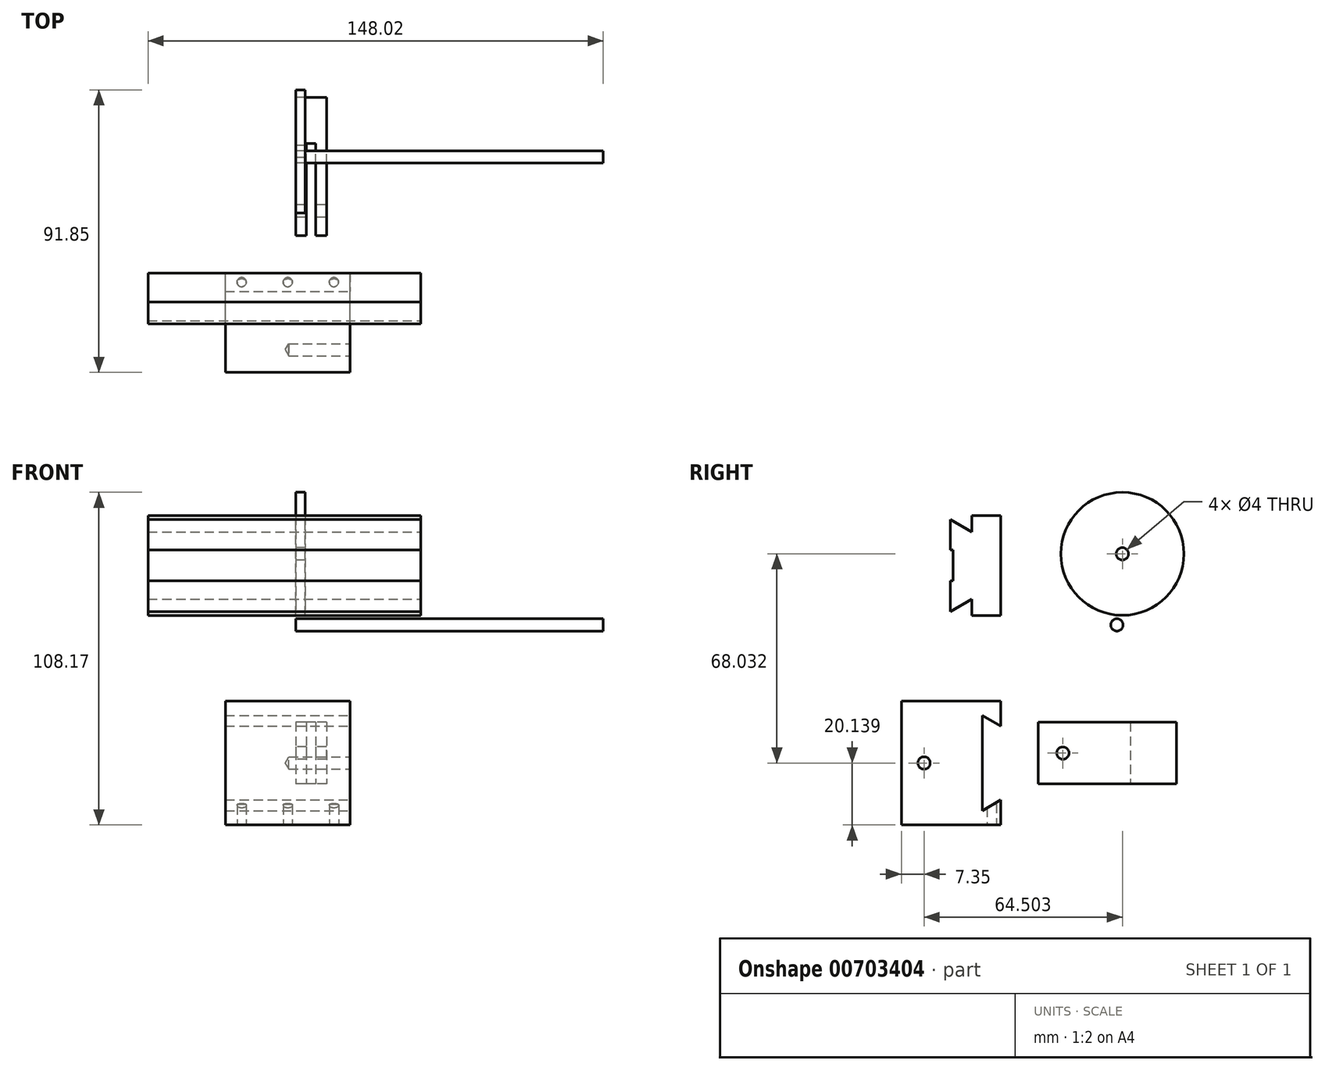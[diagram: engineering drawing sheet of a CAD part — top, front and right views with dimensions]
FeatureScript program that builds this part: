
annotation { "Feature Type Name" : "Feature", "Feature Type Description" : "" }
export const myFeature = defineFeature(function(context is Context, id is Id, definition is map)
    precondition{}
    {
        {
            var Q0;
            Q0=qCreatedBy(makeId("Front.planeOp"),FACE);
            var sketch = newSketch(context, id + "F0", { "sketchPlane" : qUnion([Q0])});
            skLineSegment(sketch, "E0.bottom", {"start": v(-48.02, 50.48) * mm, "end": v(40.65, 50.48) * mm});
            skLineSegment(sketch, "E0.top", {"start": v(-48.02, 17.98) * mm, "end": v(40.65, 17.98) * mm});
            skLineSegment(sketch, "E0.left", {"start": v(-48.02, 50.48) * mm, "end": v(-48.02, 17.98) * mm});
            skLineSegment(sketch, "E0.right", {"start": v(40.65, 50.48) * mm, "end": v(40.65, 17.98) * mm});
            skSolve(sketch);
        }
        {
            var Q0;
            Q0=makeQuery(id+"F0.imprint","IMPRINT",FACE,{"disambiguationData":[TD([[makeQuery(id+"F0.imprint","IMPRINT",EDGE,{"derivedFrom":sQuery(id+"F0.wireOp",EDGE,"E0.bottom")}),-1.0]])]});
            extrude(context, id + "F1", {"entities" : qUnion([Q0]), "depth" : 16.5 * mm, "offsetDistance" : 25 * mm});
        }
        {
            var Q0;
            Q0=qCreatedBy(makeId("Front.planeOp"),FACE);
            var sketch = newSketch(context, id + "F2", { "sketchPlane" : qUnion([Q0])});
            skLineSegment(sketch, "E1.bottom", {"start": v(-22.87, -9.87) * mm, "end": v(17.73, -9.87) * mm});
            skLineSegment(sketch, "E1.top", {"start": v(-22.87, -50.14) * mm, "end": v(17.73, -50.14) * mm});
            skLineSegment(sketch, "E1.left", {"start": v(-22.87, -9.87) * mm, "end": v(-22.87, -50.14) * mm});
            skLineSegment(sketch, "E1.right", {"start": v(17.73, -9.87) * mm, "end": v(17.73, -50.14) * mm});
            skSolve(sketch);
        }
        {
            var Q0;
            Q0=makeQuery(id+"F2.imprint","IMPRINT",FACE,{"disambiguationData":[TD([[makeQuery(id+"F2.imprint","IMPRINT",EDGE,{"derivedFrom":sQuery(id+"F2.wireOp",EDGE,"E1.bottom")}),-1.0]])]});
            extrude(context, id + "F3", {"entities" : qUnion([Q0]), "depth" : 32.35 * mm, "offsetDistance" : 25 * mm});
        }
        {
            var Q0;
            Q0=makeQuery(id+"F3.opExtrude","SWEPT_FACE",FACE,{"disambiguationData":[OSD([sQuery(id+"F2.wireOp",EDGE,"E1.right")])]});
            var sketch = newSketch(context, id + "F4", { "sketchPlane" : qUnion([Q0])});
            skLineSegment(sketch, "E2", {"start": v(0, -17.97) * mm, "end": v(-6, -14.5) * mm});
            skLineSegment(sketch, "E3", {"start": v(-6, -14.5) * mm, "end": v(-6, -45.5) * mm});
            skLineSegment(sketch, "E4", {"start": v(-6, -45.5) * mm, "end": v(0, -42.04) * mm});
            skLineSegment(sketch, "E5", {"start": v(0, -30) * mm, "end": v(-32.35, -30) * mm, "construction": true});
            skPoint(sketch, "E6", {"position": v(-25, -30) * mm});
            skPoint(sketch, "E6.positionSnap0", {"position": v(-25, -30) * mm});
            skLineSegment(sketch, "E7", {"start": v(0, -17.97) * mm, "end": v(0, -42.04) * mm});
            skSolve(sketch);
        }
        {
            var Q0;
            {var subQ0=sQuery(id+"F4.wireOp",EDGE,"E2");Q0=makeQuery(id+"F4.imprint","IMPRINT",FACE,{"disambiguationData":[TD([[makeQuery(id+"F4.imprint","IMPRINT",EDGE,{"derivedFrom":subQ0}),1.0]])]});}
            extrude(context, id + "F5", {"entities" : qUnion([Q0]), "operationType" : NewBodyOperationType.REMOVE, "endBound" : BoundingType.UP_TO_NEXT, "oppositeDirection" : true, "depth" : 25 * mm, "offsetDistance" : 25 * mm});
        }
        {
            var Q0;
            Q0=makeQuery(id+"F1.opExtrude","SWEPT_FACE",FACE,{"disambiguationData":[OSD([sQuery(id+"F0.wireOp",EDGE,"E0.right")])]});
            var sketch = newSketch(context, id + "F6", { "sketchPlane" : qUnion([Q0])});
            skLineSegment(sketch, "E8", {"start": v(-16.5, 50.48) * mm, "end": v(-9.5, 50.48) * mm, "construction": true});
            skLineSegment(sketch, "E9", {"start": v(-16.5, 50.48) * mm, "end": v(-16.5, 49.23) * mm, "construction": true});
            skLineSegment(sketch, "E10", {"start": v(-16.5, 19.23) * mm, "end": v(-16.5, 17.98) * mm, "construction": true});
            skLineSegment(sketch, "E11", {"start": v(-16.5, 17.98) * mm, "end": v(-9.5, 17.98) * mm, "construction": true});
            skLineSegment(sketch, "E12", {"start": v(-16.5, 49.23) * mm, "end": v(-9.5, 45.18) * mm});
            skLineSegment(sketch, "E13", {"start": v(-9.5, 45.18) * mm, "end": v(-9.5, 50.48) * mm});
            skLineSegment(sketch, "E14", {"start": v(-16.5, 19.23) * mm, "end": v(-9.5, 23.27) * mm});
            skLineSegment(sketch, "E15", {"start": v(-9.5, 23.27) * mm, "end": v(-9.5, 17.98) * mm});
            skLineSegment(sketch, "E16", {"start": v(-16.5, 19.23) * mm, "end": v(-16.5, 49.23) * mm});
            skSolve(sketch);
        }
        {
            var Q0;
            {var subQ0=sQuery(id+"F6.wireOp",EDGE,"E12");Q0=makeQuery(id+"F6.imprint","IMPRINT",FACE,{"disambiguationData":[TD([[makeQuery(id+"F6.imprint","IMPRINT",EDGE,{"derivedFrom":subQ0}),1.0]])]});}
            var Q1;
            {var subQ0=sQuery(id+"F6.wireOp",EDGE,"E14");Q1=makeQuery(id+"F6.imprint","IMPRINT",FACE,{"disambiguationData":[TD([[makeQuery(id+"F6.imprint","IMPRINT",EDGE,{"derivedFrom":subQ0}),-1.0]])]});}
            extrude(context, id + "F7", {"entities" : qUnion([Q0, Q1]), "operationType" : NewBodyOperationType.REMOVE, "endBound" : BoundingType.UP_TO_NEXT, "oppositeDirection" : true, "depth" : 25 * mm, "offsetDistance" : 25 * mm});
        }
        {
            var Q0;
            Q0=makeQuery(id+"F1.opExtrude","CAP_FACE",FACE,{"disambiguationData":[OSD([sQuery(id+"F0.wireOp",EDGE,"E0.bottom"),sQuery(id+"F0.wireOp",EDGE,"E0.top"),sQuery(id+"F0.wireOp",EDGE,"E0.left"),sQuery(id+"F0.wireOp",EDGE,"E0.right")])],"isStart":false});
            var sketch = newSketch(context, id + "F8", { "sketchPlane" : qUnion([Q0])});
            skLineSegment(sketch, "E17", {"start": v(-48.02, 34.23) * mm, "end": v(40.65, 34.23) * mm, "construction": true});
            skLineSegment(sketch, "E18.bottom", {"start": v(-48.02, 39.23) * mm, "end": v(40.65, 39.23) * mm});
            skLineSegment(sketch, "E18.top", {"start": v(-48.02, 29.23) * mm, "end": v(40.65, 29.23) * mm});
            skLineSegment(sketch, "E18.left", {"start": v(-48.02, 39.23) * mm, "end": v(-48.02, 29.23) * mm});
            skLineSegment(sketch, "E18.right", {"start": v(40.65, 39.23) * mm, "end": v(40.65, 29.23) * mm});
            skPoint(sketch, "E18.middle", {"position": v(-3.68, 34.23) * mm});
            skSolve(sketch);
        }
        {
            var Q0;
            Q0=makeQuery(id+"F8.imprint","IMPRINT",FACE,{"disambiguationData":[TD([[makeQuery(id+"F8.imprint","IMPRINT",EDGE,{"derivedFrom":sQuery(id+"F8.wireOp",EDGE,"E18.bottom")}),-1.0]])]});
            extrude(context, id + "F9", {"entities" : qUnion([Q0]), "operationType" : NewBodyOperationType.REMOVE, "oppositeDirection" : true, "depth" : 1 * mm, "offsetDistance" : 25 * mm});
        }
        {
            var Q0;
            Q0=makeQuery(id+"F3.opExtrude","SWEPT_FACE",FACE,{"disambiguationData":[OSD([sQuery(id+"F2.wireOp",EDGE,"E1.top")])]});
            var sketch = newSketch(context, id + "F10", { "sketchPlane" : qUnion([Q0])});
            skLineSegment(sketch, "E19", {"start": v(-22.87, 3) * mm, "end": v(17.73, 3) * mm, "construction": true});
            skPoint(sketch, "E20", {"position": v(-2.57, 3) * mm});
            skLineSegment(sketch, "E21", {"start": v(-2.57, 3) * mm, "end": v(-17.57, 3) * mm, "construction": true});
            skLineSegment(sketch, "E22", {"start": v(-2.57, 3) * mm, "end": v(12.43, 3) * mm, "construction": true});
            skSolve(sketch);
        }
        {
            var Q0;
            Q0=sQuery(id+"F10.wireOp",VERTEX,"E20");
            var Q1;
            Q1=sQuery(id+"F10.wireOp",VERTEX,"E22.end");
            var Q2;
            Q2=sQuery(id+"F10.wireOp",VERTEX,"E21.end");
            var Q3;
            Q3=makeQuery(id+"F3.opExtrude","SWEPT_BODY",BODY,{"disambiguationData":[OSD([sQuery(id+"F2.wireOp",EDGE,"E1.bottom"),sQuery(id+"F2.wireOp",EDGE,"E1.top"),sQuery(id+"F2.wireOp",EDGE,"E1.left"),sQuery(id+"F2.wireOp",EDGE,"E1.right")])]});
            hole(context, id + "F11", {"style" : HoleStyle.SIMPLE, "endStyle" : HoleEndStyle.BLIND, "holeDiameter" : 3 * mm, "majorDiameter" : 5 * mm, "holeDepth" : 6.8 * mm, "isTappedThrough" : true, "tappedDepth" : 12 * mm, "tapClearance" : 3, "locations" : qUnion([Q0, Q1, Q2]), "scope" : qUnion([Q3])});
        }
        {
            var Q0;
            Q0=sQuery(id+"F4.wireOp",VERTEX,"E6.positionSnap0");
            var Q1;
            Q1=makeQuery(id+"F3.opExtrude","SWEPT_BODY",BODY,{"disambiguationData":[OSD([sQuery(id+"F2.wireOp",EDGE,"E1.bottom"),sQuery(id+"F2.wireOp",EDGE,"E1.top"),sQuery(id+"F2.wireOp",EDGE,"E1.left"),sQuery(id+"F2.wireOp",EDGE,"E1.right")])]});
            hole(context, id + "F12", {"style" : HoleStyle.SIMPLE, "endStyle" : HoleEndStyle.BLIND, "holeDiameter" : 4 * mm, "majorDiameter" : 5 * mm, "holeDepth" : 20 * mm, "isTappedThrough" : true, "tappedDepth" : 12 * mm, "tapClearance" : 3, "locations" : qUnion([Q0]), "scope" : qUnion([Q1])});
        }
        {
            var Q0;
            Q0=qCreatedBy(makeId("Right.planeOp"),FACE);
            var sketch = newSketch(context, id + "F13", { "sketchPlane" : qUnion([Q0])});
            skLineSegment(sketch, "E23.bottom", {"start": v(12.15, -16.78) * mm, "end": v(57.15, -16.78) * mm});
            skLineSegment(sketch, "E23.top", {"start": v(12.15, -36.78) * mm, "end": v(57.15, -36.78) * mm});
            skLineSegment(sketch, "E23.left", {"start": v(12.15, -16.78) * mm, "end": v(12.15, -36.78) * mm});
            skLineSegment(sketch, "E23.right", {"start": v(57.15, -16.78) * mm, "end": v(57.15, -36.78) * mm});
            skPoint(sketch, "E24.0", {"position": v(-25, -30) * mm});
            skLineSegment(sketch, "E25", {"start": v(12.15, -26.78) * mm, "end": v(57.15, -26.78) * mm, "construction": true});
            skPoint(sketch, "E26", {"position": v(20.15, -26.78) * mm});
            skSolve(sketch);
        }
        {
            var Q0;
            Q0=makeQuery(id+"F13.imprint","IMPRINT",FACE,{"disambiguationData":[TD([[makeQuery(id+"F13.imprint","IMPRINT",EDGE,{"derivedFrom":sQuery(id+"F13.wireOp",EDGE,"E23.bottom")}),-1.0]])]});
            extrude(context, id + "F14", {"entities" : qUnion([Q0]), "depth" : 10 * mm, "offsetDistance" : 25 * mm});
        }
        {
            var Q0;
            Q0=makeQuery(id+"F14.opExtrude","SWEPT_FACE",FACE,{"disambiguationData":[OSD([sQuery(id+"F13.wireOp",EDGE,"E23.top")])]});
            var sketch = newSketch(context, id + "F15", { "sketchPlane" : qUnion([Q0])});
            skLineSegment(sketch, "E27", {"start": v(5, -12.15) * mm, "end": v(5, -57.15) * mm, "construction": true});
            skLineSegment(sketch, "E28.bottom", {"start": v(6.5, -12.15) * mm, "end": v(3.5, -12.15) * mm});
            skLineSegment(sketch, "E28.top", {"start": v(6.5, -57.15) * mm, "end": v(3.5, -57.15) * mm});
            skLineSegment(sketch, "E28.left", {"start": v(6.5, -12.15) * mm, "end": v(6.5, -57.15) * mm});
            skLineSegment(sketch, "E28.right", {"start": v(3.5, -12.15) * mm, "end": v(3.5, -57.15) * mm});
            skPoint(sketch, "E28.middle", {"position": v(5, -34.65) * mm});
            skLineSegment(sketch, "E29", {"start": v(6.5, -42.15) * mm, "end": v(3.5, -42.15) * mm});
            skSolve(sketch);
        }
        {
            var Q0;
            {var subQ0=sQuery(id+"F15.wireOp",EDGE,"E28.bottom");Q0=makeQuery(id+"F15.imprint","IMPRINT",FACE,{"disambiguationData":[TD([[makeQuery(id+"F15.imprint","IMPRINT",EDGE,{"derivedFrom":subQ0}),1.0]])]});}
            extrude(context, id + "F16", {"entities" : qUnion([Q0]), "operationType" : NewBodyOperationType.REMOVE, "endBound" : BoundingType.UP_TO_NEXT, "oppositeDirection" : true, "depth" : 25 * mm, "offsetDistance" : 25 * mm});
        }
        {
            var Q0;
            Q0=sQuery(id+"F13.wireOp",VERTEX,"E26");
            var Q1;
            Q1=makeQuery(id+"F14.opExtrude","SWEPT_BODY",BODY,{"disambiguationData":[OSD([sQuery(id+"F13.wireOp",EDGE,"E23.bottom"),sQuery(id+"F13.wireOp",EDGE,"E23.top"),sQuery(id+"F13.wireOp",EDGE,"E23.left"),sQuery(id+"F13.wireOp",EDGE,"E23.right")])]});
            hole(context, id + "F17", {"style" : HoleStyle.SIMPLE, "endStyle" : HoleEndStyle.THROUGH, "oppositeDirection" : true, "holeDiameter" : 4 * mm, "majorDiameter" : 5 * mm, "isTappedThrough" : true, "tappedDepth" : 12 * mm, "tapClearance" : 3, "locations" : qUnion([Q0]), "scope" : qUnion([Q1])});
        }
        {
            var Q0;
            Q0=qCreatedBy(makeId("Right.planeOp"),FACE);
            var sketch = newSketch(context, id + "F18", { "sketchPlane" : qUnion([Q0])});
            skCircle(sketch, "E30", {"center": v(37.73, 14.91) * mm, "radius": 2 * mm});
            skSolve(sketch);
        }
        {
            var Q0;
            Q0=makeQuery(id+"F18.imprint","IMPRINT",FACE,{"disambiguationData":[TD([[makeQuery(id+"F18.imprint","IMPRINT",EDGE,{"derivedFrom":sQuery(id+"F18.wireOp",EDGE,"E30")}),1.0]])]});
            var Q1;
            Q1=sQuery(id+"F18.wireOp",EDGE,"E30");
            extrude(context, id + "F19", {"entities" : qUnion([Q0]), "surfaceEntities" : qUnion([Q1]), "depth" : 100 * mm, "offsetDistance" : 25 * mm});
        }
        {
            var Q0;
            Q0=qCreatedBy(makeId("Right.planeOp"),FACE);
            var sketch = newSketch(context, id + "F20", { "sketchPlane" : qUnion([Q0])});
            skCircle(sketch, "E31", {"center": v(39.5, 38.03) * mm, "radius": 20 * mm});
            skSolve(sketch);
        }
        {
            var Q0;
            Q0=makeQuery(id+"F20.imprint","IMPRINT",FACE,{"disambiguationData":[TD([[makeQuery(id+"F20.imprint","IMPRINT",EDGE,{"derivedFrom":sQuery(id+"F20.wireOp",EDGE,"E31")}),1.0]])]});
            extrude(context, id + "F21", {"entities" : qUnion([Q0]), "depth" : 3 * mm, "offsetDistance" : 25 * mm});
        }
        {
            var Q0;
            Q0=sQuery(id+"F20.wireOp",VERTEX,"E31.center");
            var Q1;
            Q1=makeQuery(id+"F21.opExtrude","SWEPT_BODY",BODY,{"disambiguationData":[OSD([sQuery(id+"F20.wireOp",EDGE,"E31")])]});
            hole(context, id + "F22", {"style" : HoleStyle.SIMPLE, "endStyle" : HoleEndStyle.THROUGH, "oppositeDirection" : true, "holeDiameter" : 4 * mm, "majorDiameter" : 5 * mm, "isTappedThrough" : true, "tappedDepth" : 12 * mm, "tapClearance" : 3, "locations" : qUnion([Q0]), "scope" : qUnion([Q1])});
        }
    });
